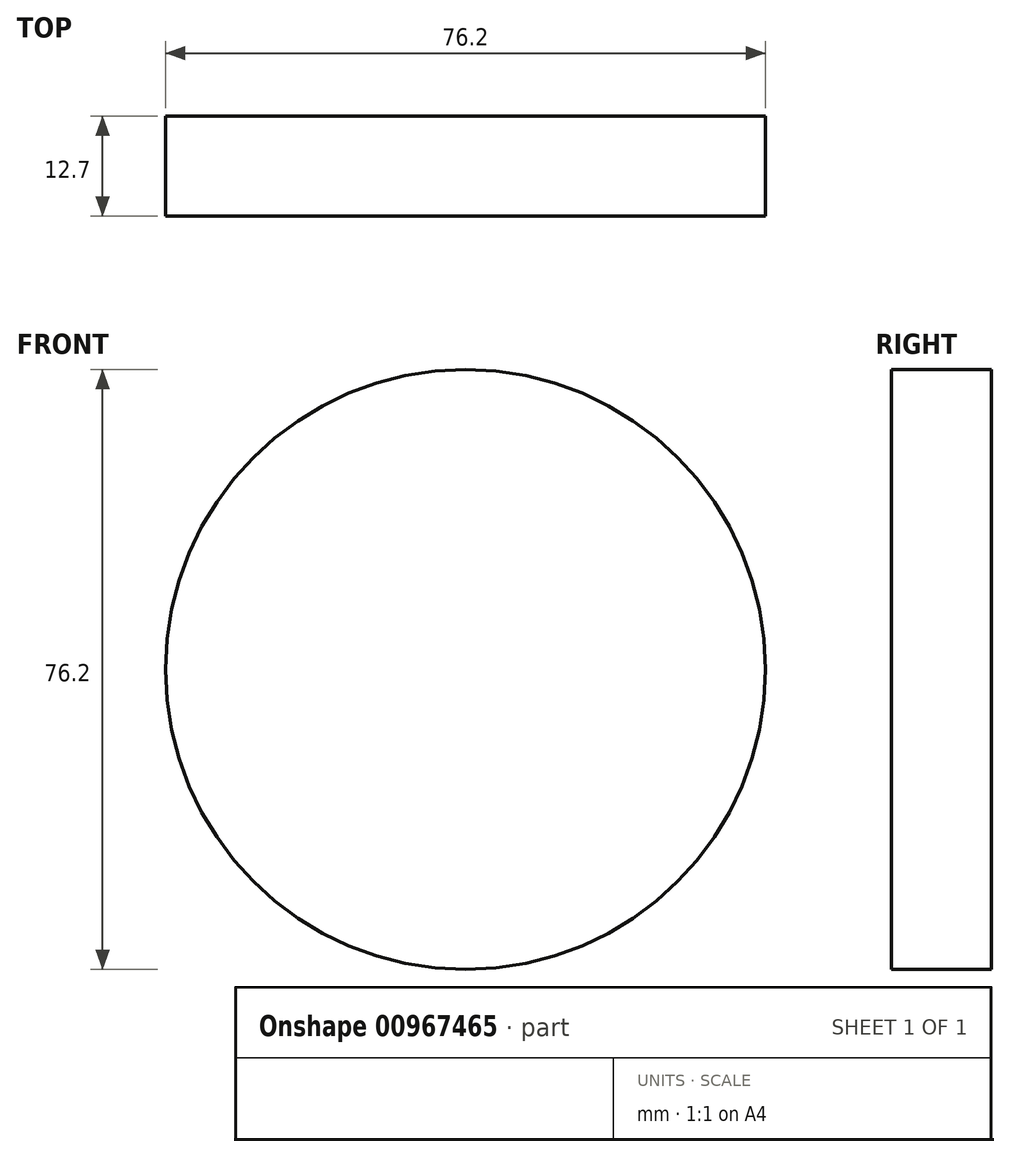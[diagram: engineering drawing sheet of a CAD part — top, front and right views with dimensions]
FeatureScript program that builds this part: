
annotation { "Feature Type Name" : "Feature", "Feature Type Description" : "" }
export const myFeature = defineFeature(function(context is Context, id is Id, definition is map)
    precondition{}
    {
        {
            var Q0;
            Q0=qCreatedBy(makeId("Front.planeOp"),FACE);
            var sketch = newSketch(context, id + "F0", { "sketchPlane" : qUnion([Q0])});
            skCircle(sketch, "E0", {"center": v(0, 0) * mm, "radius": 38.1 * mm});
            skSolve(sketch);
        }
        {
            var Q0;
            Q0=makeQuery(id+"F0.imprint","IMPRINT",FACE,{"disambiguationData":[TD([[makeQuery(id+"F0.imprint","IMPRINT",EDGE,{"derivedFrom":sQuery(id+"F0.wireOp",EDGE,"E0")}),1.0]])]});
            extrude(context, id + "F1", {"entities" : qUnion([Q0]), "depth" : 12.7 * mm, "offsetDistance" : 25.4 * mm});
        }
    });
